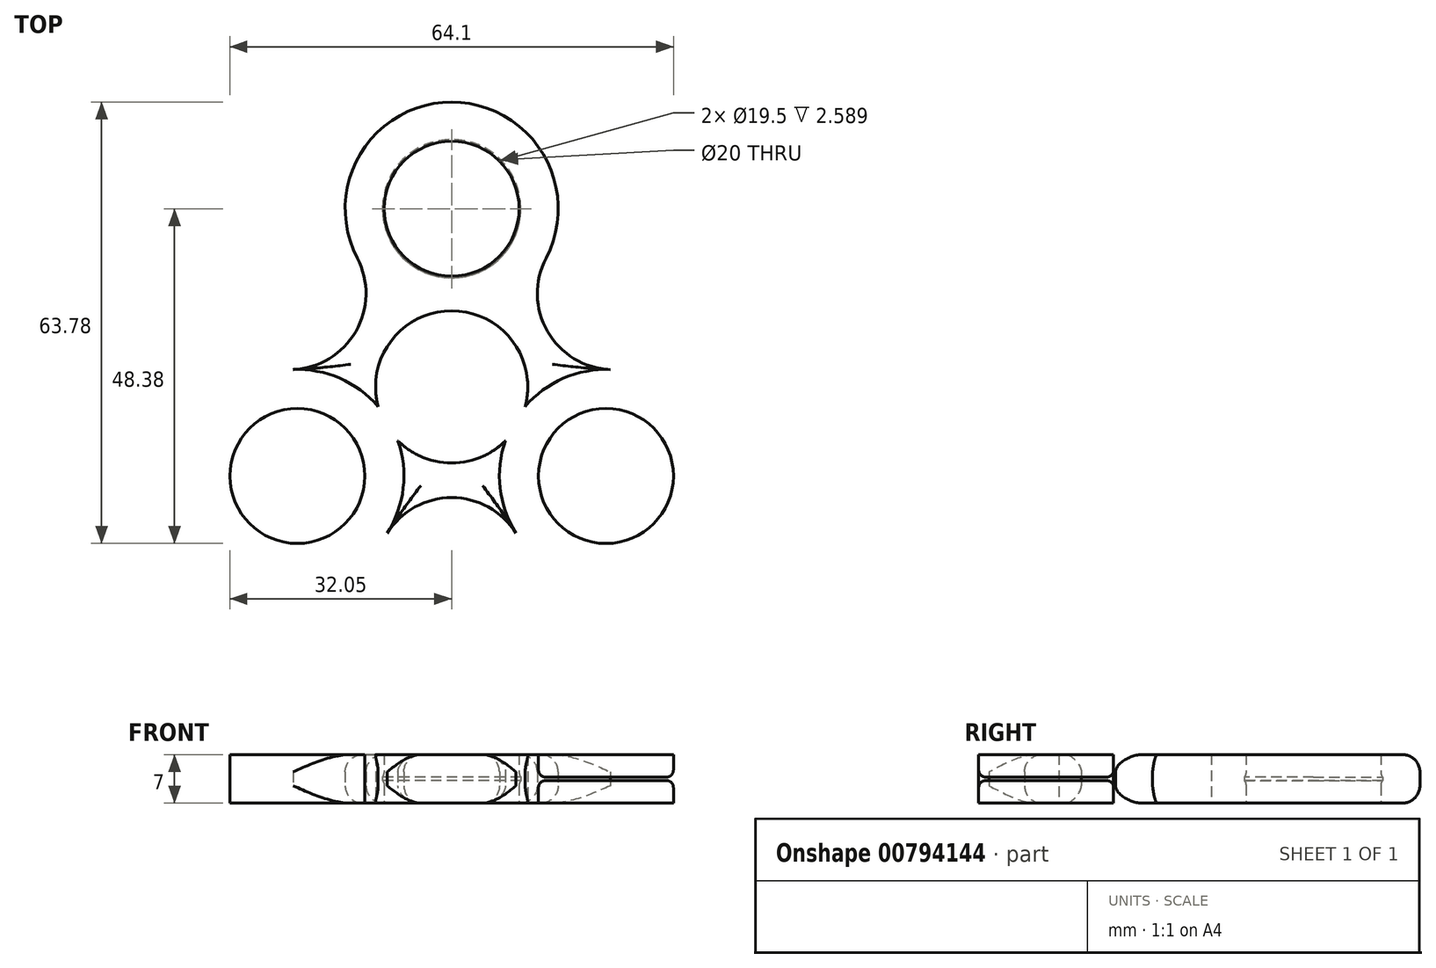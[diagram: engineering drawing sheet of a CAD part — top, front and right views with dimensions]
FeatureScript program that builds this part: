
annotation { "Feature Type Name" : "Feature", "Feature Type Description" : "" }
export const myFeature = defineFeature(function(context is Context, id is Id, definition is map)
    precondition{}
    {
        {
            var Q0;
            Q0=qCreatedBy(makeId("Top.planeOp"),FACE);
            var sketch = newSketch(context, id + "F0", { "sketchPlane" : qUnion([Q0])});
            skCircle(sketch, "E0", {"center": v(0, 0) * mm, "radius": 11 * mm});
            skCircle(sketch, "E1", {"center": v(0, 25.75) * mm, "radius": 9.75 * mm});
            skLineSegment(sketch, "E2", {"start": v(0, 0) * mm, "end": v(-39.98, 23.08) * mm, "construction": true});
            skLineSegment(sketch, "E3.MirrorCS", {"start": v(0, 0) * mm, "end": v(39.98, 23.08) * mm, "construction": true});
            skCircle(sketch, "E4.MirrorC", {"center": v(-22.3, -12.88) * mm, "radius": 9.75 * mm});
            skCircle(sketch, "E5.MirrorC", {"center": v(22.3, -12.88) * mm, "radius": 9.75 * mm});
            skLineSegment(sketch, "E6", {"start": v(0, 0) * mm, "end": v(0, -50.92) * mm, "construction": true});
            skCircle(sketch, "E7", {"center": v(-23.38, 13.5) * mm, "radius": 11 * mm});
            skCircle(sketch, "E8.MirrorC", {"center": v(23.38, 13.5) * mm, "radius": 11 * mm});
            skLineSegment(sketch, "E9.MirrorCS", {"start": v(0, 0) * mm, "end": v(39.98, -23.08) * mm, "construction": true});
            skCircle(sketch, "E10.MirrorC", {"center": v(0, -27) * mm, "radius": 11 * mm});
            skCircle(sketch, "E11", {"center": v(0, 25.75) * mm, "radius": 15.4 * mm});
            skCircle(sketch, "E12.MirrorC", {"center": v(22.3, -12.88) * mm, "radius": 15.4 * mm});
            skCircle(sketch, "E13.MirrorC", {"center": v(-22.3, -12.88) * mm, "radius": 15.4 * mm});
            skSolve(sketch);
        }
        {
            var Q0;
            Q0=makeQuery(id+"F0.imprint","IMPRINT",FACE,{"disambiguationData":[TD([[makeQuery(id+"F0.imprint","IMPRINT",EDGE,{"derivedFrom":sQuery(id+"F0.wireOp",EDGE,"E1")}),-1.0]])]});
            var Q1;
            Q1=makeQuery(id+"F0.imprint","IMPRINT",FACE,{"disambiguationData":[TD([[makeQuery(id+"F0.imprint","IMPRINT",EDGE,{"derivedFrom":sQuery(id+"F0.wireOp",EDGE,"E0")}),-1.0]])]});
            var Q2;
            Q2=makeQuery(id+"F0.imprint","IMPRINT",FACE,{"disambiguationData":[TD([[makeQuery(id+"F0.imprint","IMPRINT",EDGE,{"derivedFrom":sQuery(id+"F0.wireOp",EDGE,"E4.MirrorC")}),1.0]])]});
            var Q3;
            Q3=makeQuery(id+"F0.imprint","IMPRINT",FACE,{"disambiguationData":[TD([[makeQuery(id+"F0.imprint","IMPRINT",EDGE,{"derivedFrom":sQuery(id+"F0.wireOp",EDGE,"E5.MirrorC")}),1.0]])]});
            extrude(context, id + "F1", {"entities" : qUnion([Q0, Q1, Q2, Q3]), "endBound" : BoundingType.SYMMETRIC, "depth" : 7 * mm, "offsetDistance" : 25 * mm});
        }
        {
            var Q0;
            Q0=makeQuery(id+"F1.opExtrude","CAP_EDGE",EDGE,{"disambiguationData":[OSD([sQuery(id+"F0.wireOp",EDGE,"E11")])],"isStart":false});
            var Q1;
            Q1=makeQuery(id+"F1.opExtrude","CAP_EDGE",EDGE,{"disambiguationData":[OSD([sQuery(id+"F0.wireOp",EDGE,"E11")])],"isStart":true});
            var Q2;
            Q2=makeQuery(id+"F1.opExtrude","CAP_EDGE",EDGE,{"disambiguationData":[OSD([sQuery(id+"F0.wireOp",EDGE,"E8.MirrorC")])],"isStart":false});
            var Q3;
            Q3=makeQuery(id+"F1.opExtrude","CAP_EDGE",EDGE,{"disambiguationData":[OSD([sQuery(id+"F0.wireOp",EDGE,"E8.MirrorC")])],"isStart":true});
            var Q4;
            Q4=makeQuery(id+"F1.opExtrude","CAP_EDGE",EDGE,{"disambiguationData":[OSD([sQuery(id+"F0.wireOp",EDGE,"E12.MirrorC")])],"isStart":true});
            var Q5;
            Q5=makeQuery(id+"F1.opExtrude","CAP_EDGE",EDGE,{"disambiguationData":[OSD([sQuery(id+"F0.wireOp",EDGE,"E12.MirrorC")])],"isStart":false});
            var Q6;
            Q6=makeQuery(id+"F1.opExtrude","CAP_EDGE",EDGE,{"disambiguationData":[OSD([sQuery(id+"F0.wireOp",EDGE,"E10.MirrorC")])],"isStart":false});
            var Q7;
            Q7=makeQuery(id+"F1.opExtrude","CAP_EDGE",EDGE,{"disambiguationData":[OSD([sQuery(id+"F0.wireOp",EDGE,"E10.MirrorC")])],"isStart":true});
            var Q8;
            Q8=makeQuery(id+"F1.opExtrude","CAP_EDGE",EDGE,{"disambiguationData":[OSD([sQuery(id+"F0.wireOp",EDGE,"E13.MirrorC")])],"isStart":true});
            var Q9;
            Q9=makeQuery(id+"F1.opExtrude","CAP_EDGE",EDGE,{"disambiguationData":[OSD([sQuery(id+"F0.wireOp",EDGE,"E13.MirrorC")])],"isStart":false});
            var Q10;
            Q10=makeQuery(id+"F1.opExtrude","CAP_EDGE",EDGE,{"disambiguationData":[OSD([sQuery(id+"F0.wireOp",EDGE,"E7")])],"isStart":false});
            var Q11;
            Q11=makeQuery(id+"F1.opExtrude","CAP_EDGE",EDGE,{"disambiguationData":[OSD([sQuery(id+"F0.wireOp",EDGE,"E7")])],"isStart":true});
            fillet(context, id + "F2", {"entities" : qUnion([Q0, Q1, Q2, Q3, Q4, Q5, Q6, Q7, Q8, Q9, Q10, Q11]), "radius" : 2.5 * mm, "tangentPropagation" : true, "allowEdgeOverflow" : false});
        }
        {
            var Q0;
            Q0=qCreatedBy(makeId("Top.planeOp"),FACE);
            var sketch = newSketch(context, id + "F3", { "sketchPlane" : qUnion([Q0])});
            skCircle(sketch, "E14", {"center": v(0, 0) * mm, "radius": 11 * mm});
            skCircle(sketch, "E15", {"center": v(0, 25.75) * mm, "radius": 10 * mm});
            skLineSegment(sketch, "E16", {"start": v(0, 0) * mm, "end": v(-36.78, 21.24) * mm, "construction": true});
            skCircle(sketch, "E17.MirrorC", {"center": v(-22.3, -12.87) * mm, "radius": 10 * mm});
            skCircle(sketch, "E18.MirrorC", {"center": v(22.3, -12.87) * mm, "radius": 10 * mm});
            skSolve(sketch);
        }
        {
            var Q0;
            Q0=makeQuery(id+"F3.imprint","IMPRINT",FACE,{"disambiguationData":[TD([[makeQuery(id+"F3.imprint","IMPRINT",EDGE,{"derivedFrom":sQuery(id+"F3.wireOp",EDGE,"E15")}),1.0]])]});
            var Q1;
            Q1=makeQuery(id+"F3.imprint","IMPRINT",FACE,{"disambiguationData":[TD([[makeQuery(id+"F3.imprint","IMPRINT",EDGE,{"derivedFrom":sQuery(id+"F3.wireOp",EDGE,"E17.MirrorC")}),-1.0]])]});
            var Q2;
            Q2=makeQuery(id+"F3.imprint","IMPRINT",FACE,{"disambiguationData":[TD([[makeQuery(id+"F3.imprint","IMPRINT",EDGE,{"derivedFrom":sQuery(id+"F3.wireOp",EDGE,"E18.MirrorC")}),1.0]])]});
            extrude(context, id + "F4", {"entities" : qUnion([Q0, Q1, Q2]), "operationType" : NewBodyOperationType.REMOVE, "endBound" : BoundingType.SYMMETRIC, "depth" : 0.5 * mm, "offsetDistance" : 25 * mm});
        }
        {
            var Q0;
            Q0=makeQuery(id+"F4.boolean.opBoolean","INTERSECT",EDGE,{"derivedFrom":[makeQuery(id+"F1.opExtrude","SWEPT_FACE",FACE,{"disambiguationData":[OSD([sQuery(id+"F0.wireOp",EDGE,"E1")])]}),makeQuery(id+"F4.opExtrude","CAP_FACE",FACE,{"disambiguationData":[OSD([sQuery(id+"F3.wireOp",EDGE,"E15")])],"isStart":true})]});
            var Q1;
            Q1=makeQuery(id+"F4.boolean.opBoolean","INTERSECT",EDGE,{"derivedFrom":[makeQuery(id+"F1.opExtrude","SWEPT_FACE",FACE,{"disambiguationData":[OSD([sQuery(id+"F0.wireOp",EDGE,"E1")])]}),makeQuery(id+"F4.opExtrude","CAP_FACE",FACE,{"disambiguationData":[OSD([sQuery(id+"F3.wireOp",EDGE,"E15")])],"isStart":false})]});
            var Q2;
            Q2=makeQuery(id+"F4.boolean.opBoolean","INTERSECT",EDGE,{"derivedFrom":[makeQuery(id+"F1.opExtrude","SWEPT_FACE",FACE,{"disambiguationData":[OSD([sQuery(id+"F0.wireOp",EDGE,"E4.MirrorC")])]}),makeQuery(id+"F4.opExtrude","CAP_FACE",FACE,{"disambiguationData":[OSD([sQuery(id+"F3.wireOp",EDGE,"E17.MirrorC")])],"isStart":false})]});
            var Q3;
            Q3=makeQuery(id+"F4.boolean.opBoolean","INTERSECT",EDGE,{"derivedFrom":[makeQuery(id+"F1.opExtrude","SWEPT_FACE",FACE,{"disambiguationData":[OSD([sQuery(id+"F0.wireOp",EDGE,"E4.MirrorC")])]}),makeQuery(id+"F4.opExtrude","CAP_FACE",FACE,{"disambiguationData":[OSD([sQuery(id+"F3.wireOp",EDGE,"E17.MirrorC")])],"isStart":true})]});
            var Q4;
            Q4=makeQuery(id+"F4.boolean.opBoolean","INTERSECT",EDGE,{"derivedFrom":[makeQuery(id+"F1.opExtrude","SWEPT_FACE",FACE,{"disambiguationData":[OSD([sQuery(id+"F0.wireOp",EDGE,"E5.MirrorC")])]}),makeQuery(id+"F4.opExtrude","CAP_FACE",FACE,{"disambiguationData":[OSD([sQuery(id+"F3.wireOp",EDGE,"E18.MirrorC")])],"isStart":false})]});
            var Q5;
            Q5=makeQuery(id+"F4.boolean.opBoolean","INTERSECT",EDGE,{"derivedFrom":[makeQuery(id+"F1.opExtrude","SWEPT_FACE",FACE,{"disambiguationData":[OSD([sQuery(id+"F0.wireOp",EDGE,"E5.MirrorC")])]}),makeQuery(id+"F4.opExtrude","CAP_FACE",FACE,{"disambiguationData":[OSD([sQuery(id+"F3.wireOp",EDGE,"E18.MirrorC")])],"isStart":true})]});
            fillet(context, id + "F5", {"entities" : qUnion([Q0, Q1, Q2, Q3, Q4, Q5]), "radius" : 1 * mm, "tangentPropagation" : true, "allowEdgeOverflow" : false});
        }
    });
